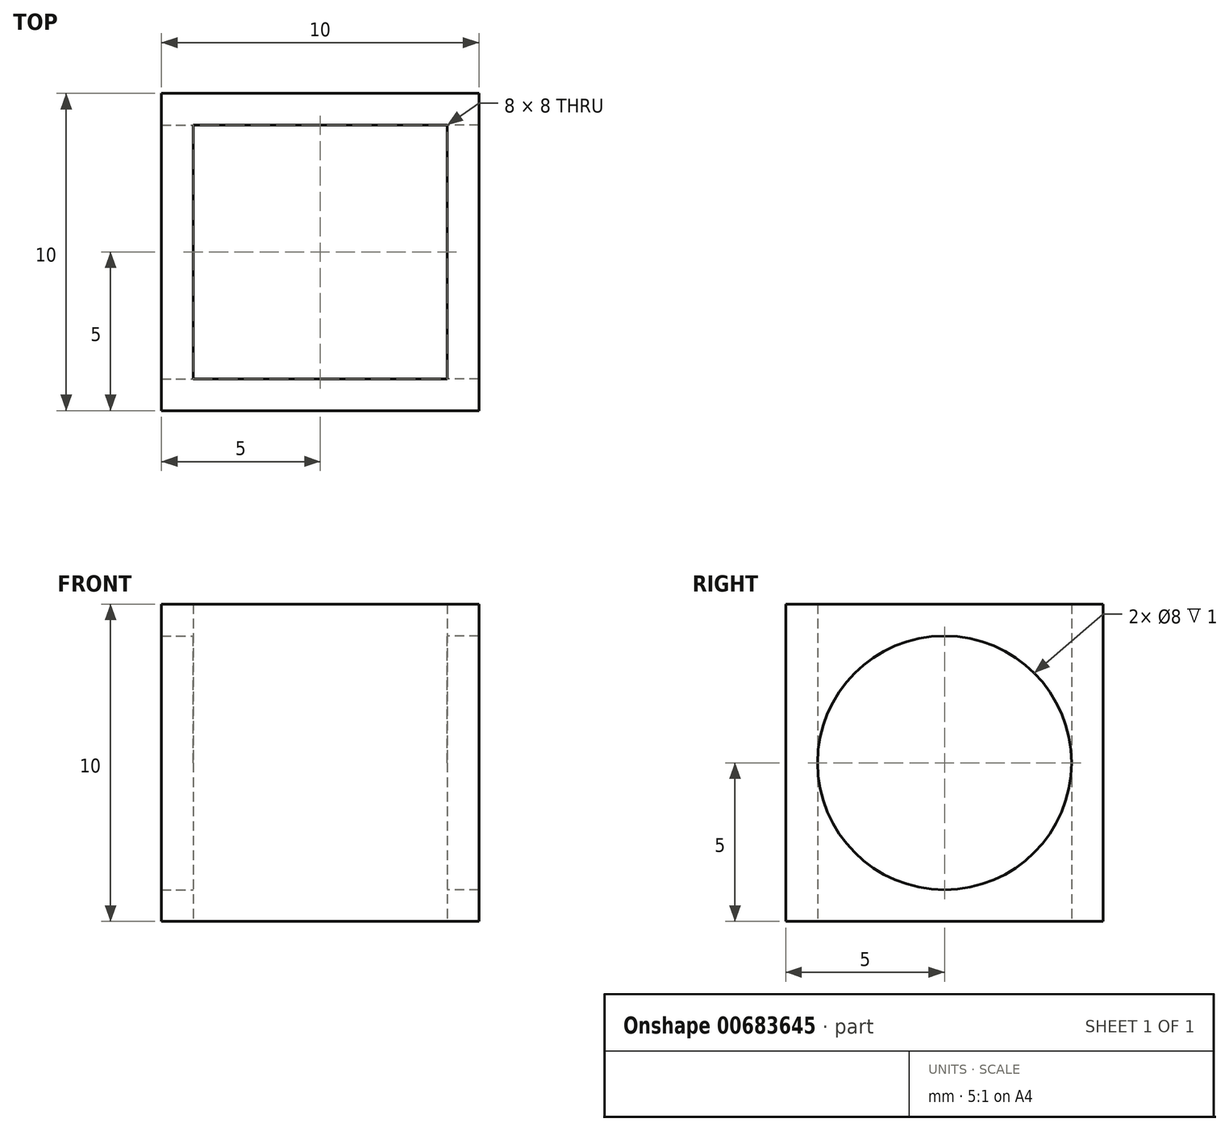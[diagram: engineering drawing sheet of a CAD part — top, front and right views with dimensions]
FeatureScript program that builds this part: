
annotation { "Feature Type Name" : "Feature", "Feature Type Description" : "" }
export const myFeature = defineFeature(function(context is Context, id is Id, definition is map)
    precondition{}
    {
        {
            var Q0;
            Q0=qCreatedBy(makeId("Front.planeOp"),FACE);
            var sketch = newSketch(context, id + "F0", { "sketchPlane" : qUnion([Q0])});
            skLineSegment(sketch, "E0.bottom", {"start": v(5, 5) * mm, "end": v(-5, 5) * mm});
            skLineSegment(sketch, "E0.top", {"start": v(5, -5) * mm, "end": v(-5, -5) * mm});
            skLineSegment(sketch, "E0.left", {"start": v(5, 5) * mm, "end": v(5, -5) * mm});
            skLineSegment(sketch, "E0.right", {"start": v(-5, 5) * mm, "end": v(-5, -5) * mm});
            skSolve(sketch);
        }
        {
            var Q0;
            Q0=makeQuery(id+"F0.imprint","IMPRINT",FACE,{"disambiguationData":[TD([[makeQuery(id+"F0.imprint","IMPRINT",EDGE,{"derivedFrom":sQuery(id+"F0.wireOp",EDGE,"E0.bottom")}),1.0]])]});
            extrude(context, id + "F1", {"entities" : qUnion([Q0]), "endBound" : BoundingType.SYMMETRIC, "depth" : 10 * mm, "offsetDistance" : 25.4 * mm});
        }
        {
            var Q0;
            Q0=makeQuery(id+"F1.opExtrude","SWEPT_FACE",FACE,{"disambiguationData":[OSD([sQuery(id+"F0.wireOp",EDGE,"E0.bottom")])]});
            var Q1;
            Q1=makeQuery(id+"F1.opExtrude","SWEPT_FACE",FACE,{"disambiguationData":[OSD([sQuery(id+"F0.wireOp",EDGE,"E0.top")])]});
            shell(context, id + "F2", {"entities" : qUnion([Q0, Q1]), "thickness" : 1 * mm});
        }
        {
            var Q0;
            Q0=qCreatedBy(makeId("Right.planeOp"),FACE);
            var sketch = newSketch(context, id + "F3", { "sketchPlane" : qUnion([Q0])});
            skPoint(sketch, "E1", {"position": v(0, 0) * mm});
            skPoint(sketch, "E2", {"position": v(-634.97, 3.13) * mm});
            skSolve(sketch);
        }
        {
            var Q0;
            Q0=sQuery(id+"F3.wireOp",VERTEX,"E1");
            var Q1;
            Q1=makeQuery(id+"F1.opExtrude","SWEPT_BODY",BODY,{"disambiguationData":[OSD([sQuery(id+"F0.wireOp",EDGE,"E0.bottom"),sQuery(id+"F0.wireOp",EDGE,"E0.top"),sQuery(id+"F0.wireOp",EDGE,"E0.left"),sQuery(id+"F0.wireOp",EDGE,"E0.right")])]});
            hole(context, id + "F4", {"style" : HoleStyle.SIMPLE, "endStyle" : HoleEndStyle.THROUGH, "holeDiameter" : 8 * mm, "majorDiameter" : 6.35 * mm, "isTappedThrough" : true, "tappedDepth" : 12.7 * mm, "tapClearance" : 3, "locations" : qUnion([Q0]), "scope" : qUnion([Q1])});
        }
        {
            var Q0;
            Q0=sQuery(id+"F3.wireOp",VERTEX,"E1");
            var Q1;
            Q1=makeQuery(id+"F1.opExtrude","SWEPT_BODY",BODY,{"disambiguationData":[OSD([sQuery(id+"F0.wireOp",EDGE,"E0.bottom"),sQuery(id+"F0.wireOp",EDGE,"E0.top"),sQuery(id+"F0.wireOp",EDGE,"E0.left"),sQuery(id+"F0.wireOp",EDGE,"E0.right")])]});
            hole(context, id + "F5", {"style" : HoleStyle.SIMPLE, "endStyle" : HoleEndStyle.THROUGH, "oppositeDirection" : true, "holeDiameter" : 8 * mm, "majorDiameter" : 6.35 * mm, "isTappedThrough" : true, "tappedDepth" : 12.7 * mm, "tapClearance" : 3, "locations" : qUnion([Q0]), "scope" : qUnion([Q1])});
        }
    });
